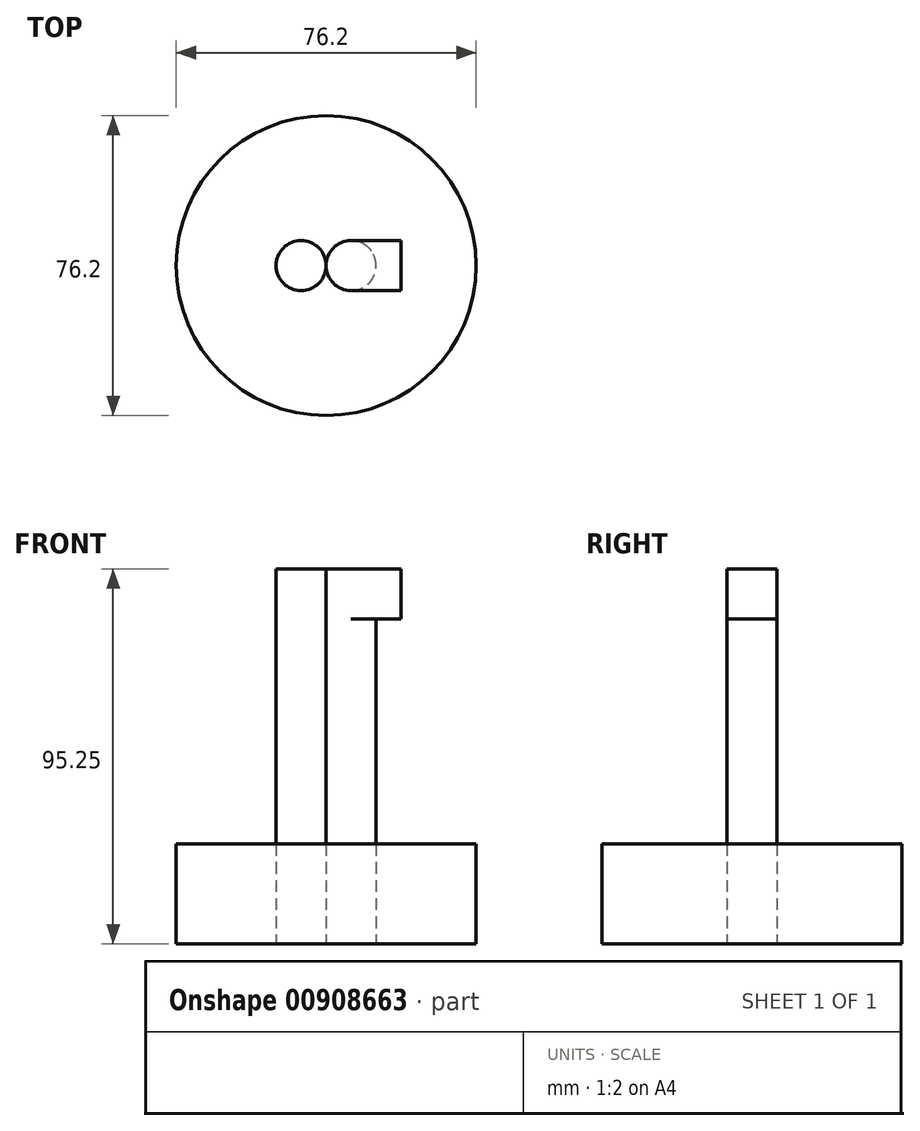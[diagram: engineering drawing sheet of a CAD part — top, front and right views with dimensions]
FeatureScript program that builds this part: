
annotation { "Feature Type Name" : "Feature", "Feature Type Description" : "" }
export const myFeature = defineFeature(function(context is Context, id is Id, definition is map)
    precondition{}
    {
        {
            var Q0;
            Q0=qCreatedBy(makeId("Top.planeOp"),FACE);
            var sketch = newSketch(context, id + "F0", { "sketchPlane" : qUnion([Q0])});
            skCircle(sketch, "E0", {"center": v(0, 0) * mm, "radius": 38.1 * mm});
            skCircle(sketch, "E1", {"center": v(-6.35, 0) * mm, "radius": 6.35 * mm});
            skCircle(sketch, "E2", {"center": v(6.35, 0) * mm, "radius": 6.35 * mm});
            skSolve(sketch);
        }
        {
            var Q0;
            Q0=makeQuery(id+"F0.imprint","IMPRINT",FACE,{"disambiguationData":[TD([[makeQuery(id+"F0.imprint","IMPRINT",EDGE,{"derivedFrom":sQuery(id+"F0.wireOp",EDGE,"E0")}),1.0]])]});
            var Q1;
            Q1=makeQuery(id+"F0.imprint","IMPRINT",FACE,{"disambiguationData":[TD([[makeQuery(id+"F0.imprint","IMPRINT",EDGE,{"derivedFrom":sQuery(id+"F0.wireOp",EDGE,"E2")}),1.0]])]});
            var Q2;
            Q2=makeQuery(id+"F0.imprint","IMPRINT",FACE,{"disambiguationData":[TD([[makeQuery(id+"F0.imprint","IMPRINT",EDGE,{"derivedFrom":sQuery(id+"F0.wireOp",EDGE,"E1")}),1.0]])]});
            extrude(context, id + "F1", {"entities" : qUnion([Q0, Q1, Q2]), "depth" : 25.4 * mm, "offsetDistance" : 25.4 * mm});
        }
        {
            var Q0;
            Q0=makeQuery(id+"F0.imprint","IMPRINT",FACE,{"disambiguationData":[TD([[makeQuery(id+"F0.imprint","IMPRINT",EDGE,{"derivedFrom":sQuery(id+"F0.wireOp",EDGE,"E2")}),1.0]])]});
            var Q1;
            Q1=makeQuery(id+"F0.imprint","IMPRINT",FACE,{"disambiguationData":[TD([[makeQuery(id+"F0.imprint","IMPRINT",EDGE,{"derivedFrom":sQuery(id+"F0.wireOp",EDGE,"E1")}),1.0]])]});
            var Q2;
            Q2=qSketchRegion(id+"F4",true);
            extrude(context, id + "F2", {"entities" : qUnion([Q0, Q1, Q2]), "depth" : 95.25 * mm, "offsetDistance" : 25.4 * mm});
        }
        {
            var Q0;
            Q0=qCreatedBy(makeId("Right.planeOp"),FACE);
            cPlane(context, id + "F3", {"entities" : qUnion([Q0]), "cplaneType" : CPlaneType.OFFSET, "offset" : 6.35 * mm, "width" : 152.4 * mm, "height" : 152.4 * mm});
        }
        {
            var Q0;
            Q0=qCreatedBy(id+"F3.planeOp",FACE);
            var sketch = newSketch(context, id + "F4", { "sketchPlane" : qUnion([Q0])});
            skLineSegment(sketch, "E3.bottom", {"start": v(6.35, 95.25) * mm, "end": v(-6.35, 95.25) * mm});
            skLineSegment(sketch, "E3.top", {"start": v(6.35, 82.55) * mm, "end": v(-6.35, 82.55) * mm});
            skLineSegment(sketch, "E3.left", {"start": v(6.35, 95.25) * mm, "end": v(6.35, 82.55) * mm});
            skLineSegment(sketch, "E3.right", {"start": v(-6.35, 95.25) * mm, "end": v(-6.35, 82.55) * mm});
            skPoint(sketch, "E3.middle", {"position": v(0, 88.9) * mm});
            skSolve(sketch);
        }
        {
            var Q0;
            Q0=qSketchRegion(id+"F4",true);
            extrude(context, id + "F5", {"entities" : qUnion([Q0]), "operationType" : NewBodyOperationType.ADD, "depth" : 12.7 * mm, "offsetDistance" : 25.4 * mm});
        }
    });
